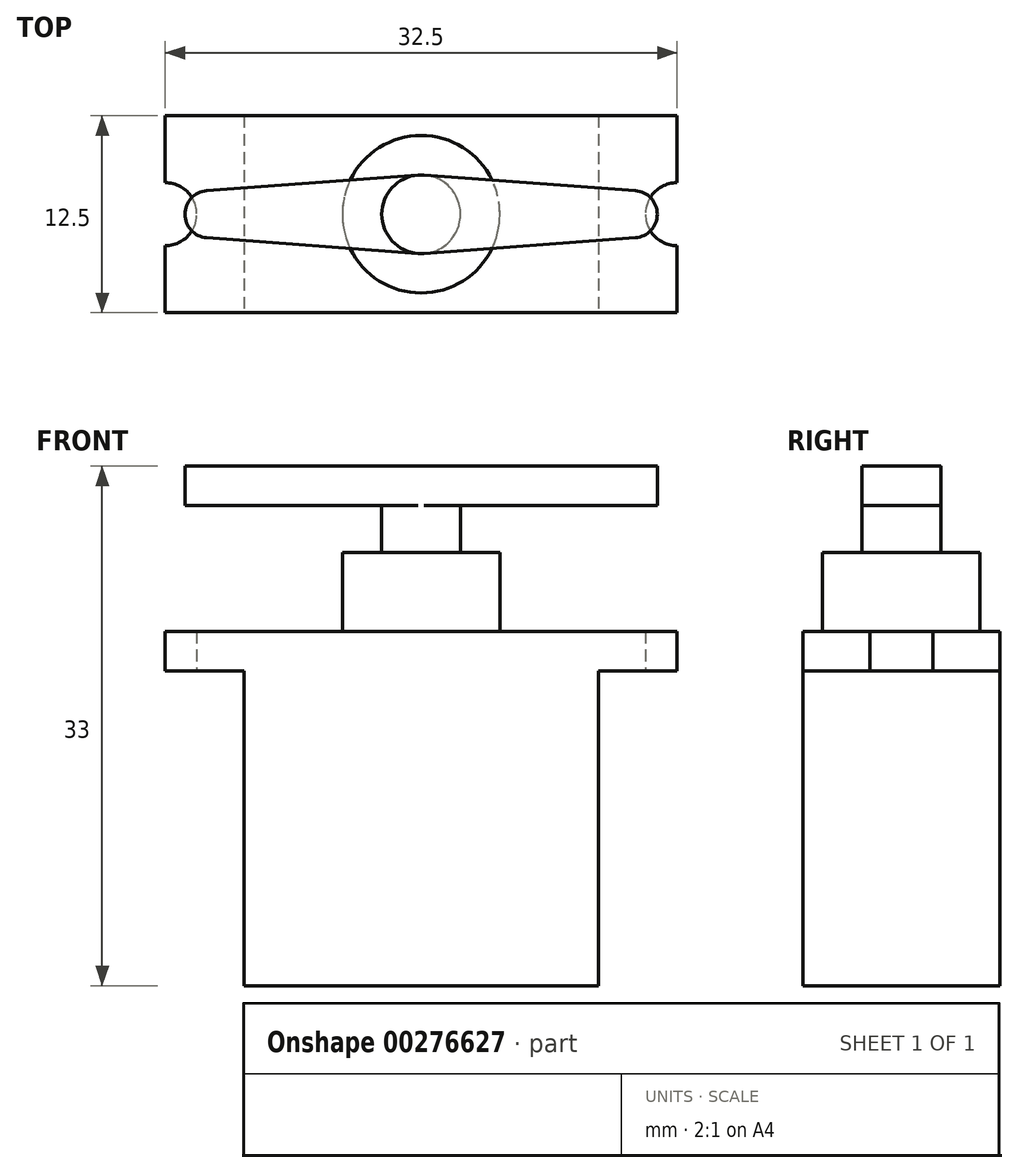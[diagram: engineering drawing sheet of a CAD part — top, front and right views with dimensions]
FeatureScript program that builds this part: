
annotation { "Feature Type Name" : "Feature", "Feature Type Description" : "" }
export const myFeature = defineFeature(function(context is Context, id is Id, definition is map)
    precondition{}
    {
        {
            var Q0;
            Q0=qCreatedBy(makeId("Top.planeOp"),FACE);
            var sketch = newSketch(context, id + "F0", { "sketchPlane" : qUnion([Q0])});
            skLineSegment(sketch, "E0.bottom", {"start": v(11.25, 6.25) * mm, "end": v(-11.25, 6.25) * mm});
            skLineSegment(sketch, "E0.top", {"start": v(11.25, -6.25) * mm, "end": v(-11.25, -6.25) * mm});
            skLineSegment(sketch, "E0.left", {"start": v(11.25, 6.25) * mm, "end": v(11.25, -6.25) * mm});
            skLineSegment(sketch, "E0.right", {"start": v(-11.25, 6.25) * mm, "end": v(-11.25, -6.25) * mm});
            skPoint(sketch, "E0.middle", {"position": v(0, 0) * mm});
            skSolve(sketch);
        }
        {
            var Q0;
            Q0 = qSketchRegion(id + "F0", true);
            extrude(context, id + "F1", {"entities" : qUnion([Q0]), "depth" : 20 * mm});
        }
        {
            var Q0;
            Q0=makeQuery(id+"F1.opExtrude","CAP_FACE",FACE,{"disambiguationData":[OSD([sQuery(id+"F0.wireOp",EDGE,"E0.bottom"),sQuery(id+"F0.wireOp",EDGE,"E0.top"),sQuery(id+"F0.wireOp",EDGE,"E0.left"),sQuery(id+"F0.wireOp",EDGE,"E0.right")])],"isStart":false});
            var sketch = newSketch(context, id + "F2", { "sketchPlane" : qUnion([Q0])});
            skLineSegment(sketch, "E1.bottom", {"start": v(16.25, 6.25) * mm, "end": v(-16.25, 6.25) * mm});
            skLineSegment(sketch, "E1.top", {"start": v(16.25, -6.25) * mm, "end": v(-16.25, -6.25) * mm});
            skLineSegment(sketch, "E1.left", {"start": v(16.25, 6.25) * mm, "end": v(16.25, 2) * mm});
            skLineSegment(sketch, "E1.right", {"start": v(-16.25, 6.25) * mm, "end": v(-16.25, 2) * mm});
            skPoint(sketch, "E1.middle", {"position": v(0, 0) * mm});
            skArc(sketch, "E2", {"start": v(-16.25, -2) * mm, "mid": v(-14.25, 0) * mm, "end": v(-16.25, 2) * mm});
            skArc(sketch, "E3", {"start": v(16.25, 2) * mm, "mid": v(14.25, 0) * mm, "end": v(16.25, -2) * mm});
            skLineSegment(sketch, "E4.trimOffspring", {"start": v(-16.25, -2) * mm, "end": v(-16.25, -6.25) * mm});
            skLineSegment(sketch, "E5.trimOffspring", {"start": v(16.25, -2) * mm, "end": v(16.25, -6.25) * mm});
            skSolve(sketch);
        }
        {
            var Q0;
            Q0 = qSketchRegion(id + "F2", true);
            extrude(context, id + "F3", {"entities" : qUnion([Q0]), "operationType" : NewBodyOperationType.ADD, "depth" : 2.5 * mm});
        }
        {
            var Q0;
            Q0=qCreatedBy(makeId("Front.planeOp"),FACE);
            var sketch = newSketch(context, id + "F4", { "sketchPlane" : qUnion([Q0])});
            skLineSegment(sketch, "E6.0", {"start": v(16.25, 22.5) * mm, "end": v(-16.25, 22.5) * mm});
            skLineSegment(sketch, "E7", {"start": v(0, 22.5) * mm, "end": v(0, 30.5) * mm});
            skPoint(sketch, "E7.endSnap0", {"position": v(0, 22.5) * mm});
            skLineSegment(sketch, "E8", {"start": v(0, 30.5) * mm, "end": v(2.5, 30.5) * mm});
            skLineSegment(sketch, "E9", {"start": v(2.5, 30.5) * mm, "end": v(2.5, 27.5) * mm});
            skLineSegment(sketch, "E10", {"start": v(2.5, 27.5) * mm, "end": v(5, 27.5) * mm});
            skLineSegment(sketch, "E11", {"start": v(5, 27.5) * mm, "end": v(5, 22.5) * mm});
            skLineSegment(sketch, "E12", {"start": v(5, 22.5) * mm, "end": v(0, 22.5) * mm});
            skSolve(sketch);
        }
        {
            var Q0;
            Q0 = qSketchRegion(id + "F4", true);
            var Q1;
            Q1=sQuery(id+"F4.wireOp",EDGE,"E7");
            revolve(context, id + "F5", {"operationType" : NewBodyOperationType.ADD, "entities" : qUnion([Q0]), "axis" : qUnion([Q1]), "revolveType" : RevolveType.FULL});
        }
        {
            var Q0;
            Q0=makeQuery(id+"F5.opRevolve","SWEPT_FACE",FACE,{"disambiguationData":[OSD([sQuery(id+"F4.wireOp",EDGE,"E8")])]});
            var sketch = newSketch(context, id + "F6", { "sketchPlane" : qUnion([Q0])});
            skLineSegment(sketch, "E13", {"start": v(0, 0) * mm, "end": v(15, 0) * mm, "construction": true});
            skArc(sketch, "E14", {"start": v(13.61, -1.5) * mm, "mid": v(15, 0) * mm, "end": v(13.61, 1.5) * mm});
            skCircle(sketch, "E15", {"center": v(0, 0) * mm, "radius": 1.48 * mm});
            skCircle(sketch, "E16.0", {"center": v(0, 0) * mm, "radius": 2.5 * mm});
            skLineSegment(sketch, "E17", {"start": v(0.19, 2.5) * mm, "end": v(13.61, 1.5) * mm});
            skLineSegment(sketch, "E18.MirrorCS", {"start": v(0.19, -2.5) * mm, "end": v(13.61, -1.5) * mm});
            skLineSegment(sketch, "E19", {"start": v(0, 0) * mm, "end": v(0, 2.5) * mm, "construction": true});
            skLineSegment(sketch, "E20.MirrorCS", {"start": v(-0.19, 2.5) * mm, "end": v(-13.61, 1.5) * mm});
            skArc(sketch, "E21.MirrorC", {"start": v(-13.61, -1.5) * mm, "mid": v(-15, 0) * mm, "end": v(-13.61, 1.5) * mm});
            skLineSegment(sketch, "E22.MirrorCS", {"start": v(-0.19, -2.5) * mm, "end": v(-13.61, -1.5) * mm});
            skSolve(sketch);
        }
        {
            var Q0;
            Q0 = qSketchRegion(id + "F6", true);
            var Q1;
            Q1=makeQuery(id+"F6.imprint","IMPRINT",FACE,{"disambiguationData":[TD([[makeQuery(id+"F6.imprint","IMPRINT",EDGE,{"derivedFrom":sQuery(id+"F6.wireOp",EDGE,"E15")}),1.0]])]});
            extrude(context, id + "F7", {"entities" : qUnion([Q0, Q1]), "operationType" : NewBodyOperationType.ADD, "depth" : 2.5 * mm});
        }
    });
